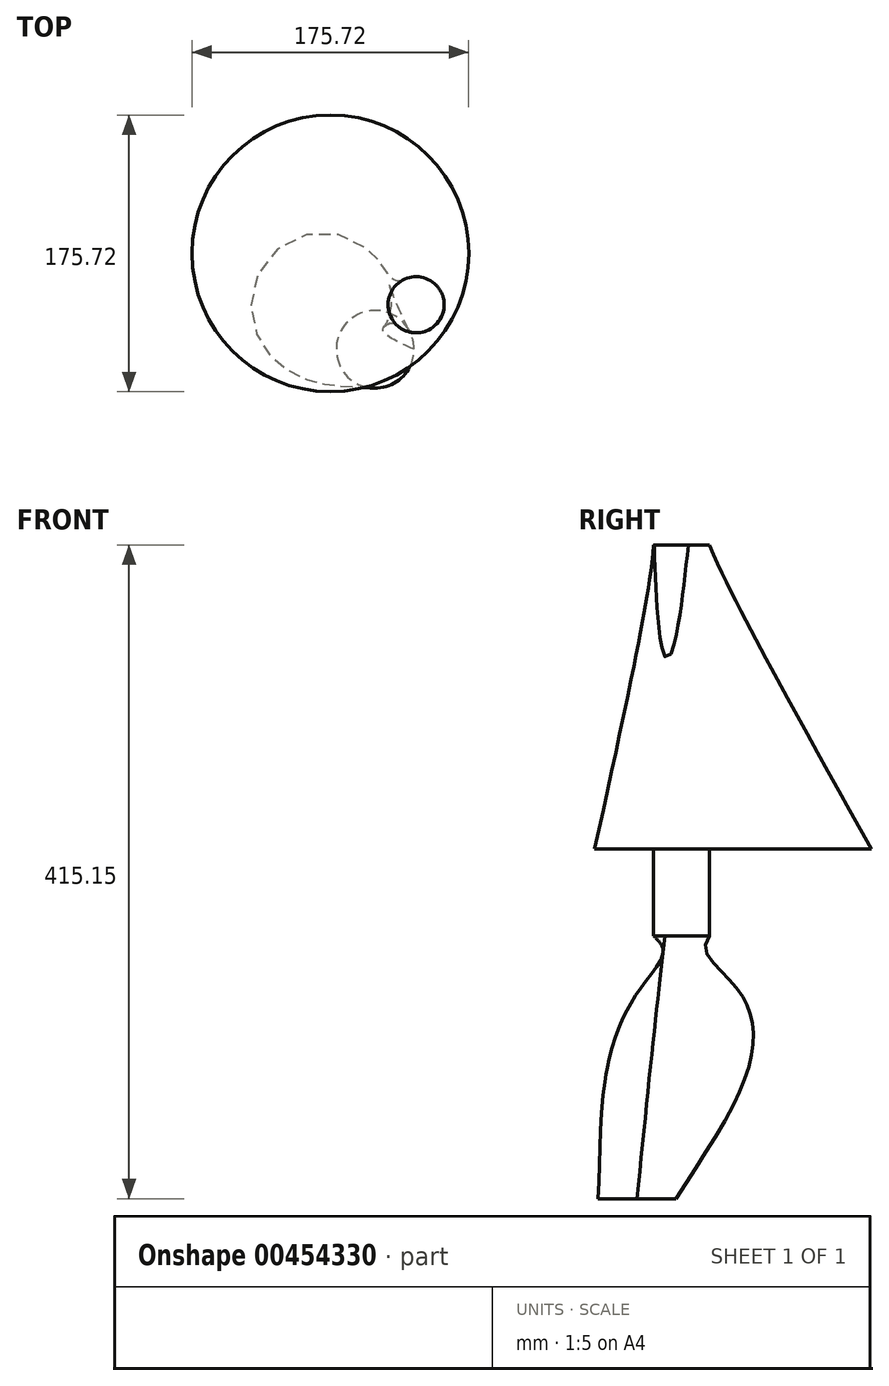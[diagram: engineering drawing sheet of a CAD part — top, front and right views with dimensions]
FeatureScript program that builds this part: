
annotation { "Feature Type Name" : "Feature", "Feature Type Description" : "" }
export const myFeature = defineFeature(function(context is Context, id is Id, definition is map)
    precondition{}
    {
        {
            var Q0;
            Q0=qCreatedBy(makeId("Top.planeOp"),FACE);
            var sketch = newSketch(context, id + "F0", { "sketchPlane" : qUnion([Q0])});
            skCircle(sketch, "E0", {"center": v(-10.32, -10.5) * mm, "radius": 24.69 * mm});
            skPoint(sketch, "E0.first.point", {"position": v(-33.37, -1.66) * mm});
            skPoint(sketch, "E0.second.point", {"position": v(13.46, -17.15) * mm});
            skPoint(sketch, "E0.third.point", {"position": v(-15.49, 13.64) * mm});
            skSolve(sketch);
        }
        {
            var Q0;
            Q0=qCreatedBy(makeId("Top.planeOp"),FACE);
            cPlane(context, id + "F1", {"entities" : qUnion([Q0]), "cplaneType" : CPlaneType.OFFSET, "offset" : 127 * mm, "width" : 152.4 * mm, "height" : 152.4 * mm});
        }
        {
            var Q0;
            Q0=qCreatedBy(id+"F1.planeOp",FACE);
            var sketch = newSketch(context, id + "F2", { "sketchPlane" : qUnion([Q0])});
            skCircle(sketch, "E1", {"center": v(-34.27, 22.26) * mm, "radius": 34.97 * mm});
            skSolve(sketch);
        }
        {
            var Q0;
            Q0=qCreatedBy(id+"F1.planeOp",FACE);
            cPlane(context, id + "F3", {"entities" : qUnion([Q0]), "cplaneType" : CPlaneType.OFFSET, "offset" : 40 * mm, "width" : 150 * mm, "height" : 150 * mm});
        }
        {
            var Q0;
            Q0=qCreatedBy(id+"F3.planeOp",FACE);
            var sketch = newSketch(context, id + "F4", { "sketchPlane" : qUnion([Q0])});
            skCircle(sketch, "E2", {"center": v(15.71, 17.78) * mm, "radius": 17.8 * mm});
            skPoint(sketch, "E2.first.point", {"position": v(14.88, 35.56) * mm});
            skPoint(sketch, "E2.second.point", {"position": v(16.54, 0) * mm});
            skPoint(sketch, "E2.third.point", {"position": v(14.88, 0) * mm});
            skSolve(sketch);
        }
        {
            var Q0;
            Q0=makeQuery(id+"F0.imprint","IMPRINT",FACE,{"disambiguationData":[TD([[makeQuery(id+"F0.imprint","IMPRINT",EDGE,{"derivedFrom":sQuery(id+"F0.wireOp",EDGE,"E0")}),1.0]])]});
            var Q1;
            Q1=makeQuery(id+"F2.imprint","IMPRINT",FACE,{"disambiguationData":[TD([[makeQuery(id+"F2.imprint","IMPRINT",EDGE,{"derivedFrom":sQuery(id+"F2.wireOp",EDGE,"E1")}),1.0]])]});
            var Q2;
            Q2=makeQuery(id+"F4.imprint","IMPRINT",FACE,{"disambiguationData":[TD([[makeQuery(id+"F4.imprint","IMPRINT",EDGE,{"derivedFrom":sQuery(id+"F4.wireOp",EDGE,"E2")}),1.0]])]});
            loft(context, id + "F5", {"sheetProfilesArray" : [{ "sheetProfileEntities" : qUnion([Q0]) }, { "sheetProfileEntities" : qUnion([Q1]) }, { "sheetProfileEntities" : qUnion([Q2]) }]});
        }
        {
            var Q0;
            Q0=makeQuery(id+"F5.opLoft","CAP_FACE",FACE,{"disambiguationData":[OSD([makeQuery(id+"F4.imprint","IMPRINT",FACE,{"disambiguationData":[TD([[makeQuery(id+"F4.imprint","IMPRINT",EDGE,{"derivedFrom":sQuery(id+"F4.wireOp",EDGE,"E2")}),1.0]])]})])],"isStart":true});
            extrude(context, id + "F6", {"entities" : qUnion([Q0]), "operationType" : NewBodyOperationType.ADD, "endBound" : BoundingType.THROUGH_ALL, "depth" : 26 * mm});
        }
        {
            var Q0;
            Q0=qCreatedBy(id+"F3.planeOp",FACE);
            cPlane(context, id + "F7", {"entities" : qUnion([Q0]), "cplaneType" : CPlaneType.OFFSET, "offset" : 55 * mm, "width" : 150 * mm, "height" : 150 * mm});
        }
        {
            var Q0;
            Q0=qCreatedBy(id+"F7.planeOp",FACE);
            var sketch = newSketch(context, id + "F8", { "sketchPlane" : qUnion([Q0])});
            skCircle(sketch, "E3", {"center": v(-38.74, 50.5) * mm, "radius": 87.86 * mm});
            skSolve(sketch);
        }
        {
            var Q1;
            Q1=makeQuery(id+"F8.imprint","IMPRINT",FACE,{"disambiguationData":[TD([[makeQuery(id+"F8.imprint","IMPRINT",EDGE,{"derivedFrom":sQuery(id+"F8.wireOp",EDGE,"E3")}),1.0]])]});
            var Q2;
            Q2=makeQuery(id+"F6.opExtrude","CAP_FACE",FACE,{"disambiguationData":[OSD([makeQuery(id+"F4.imprint","IMPRINT",FACE,{"disambiguationData":[TD([[makeQuery(id+"F4.imprint","IMPRINT",EDGE,{"derivedFrom":sQuery(id+"F4.wireOp",EDGE,"E2")}),1.0]])]})])],"isStart":false});
            loft(context, id + "F9", {"operationType" : NewBodyOperationType.ADD, "sheetProfilesArray" : [{ "sheetProfileEntities" : qUnion([Q1]) }, { "sheetProfileEntities" : qUnion([Q2]) }]});
        }
    });
